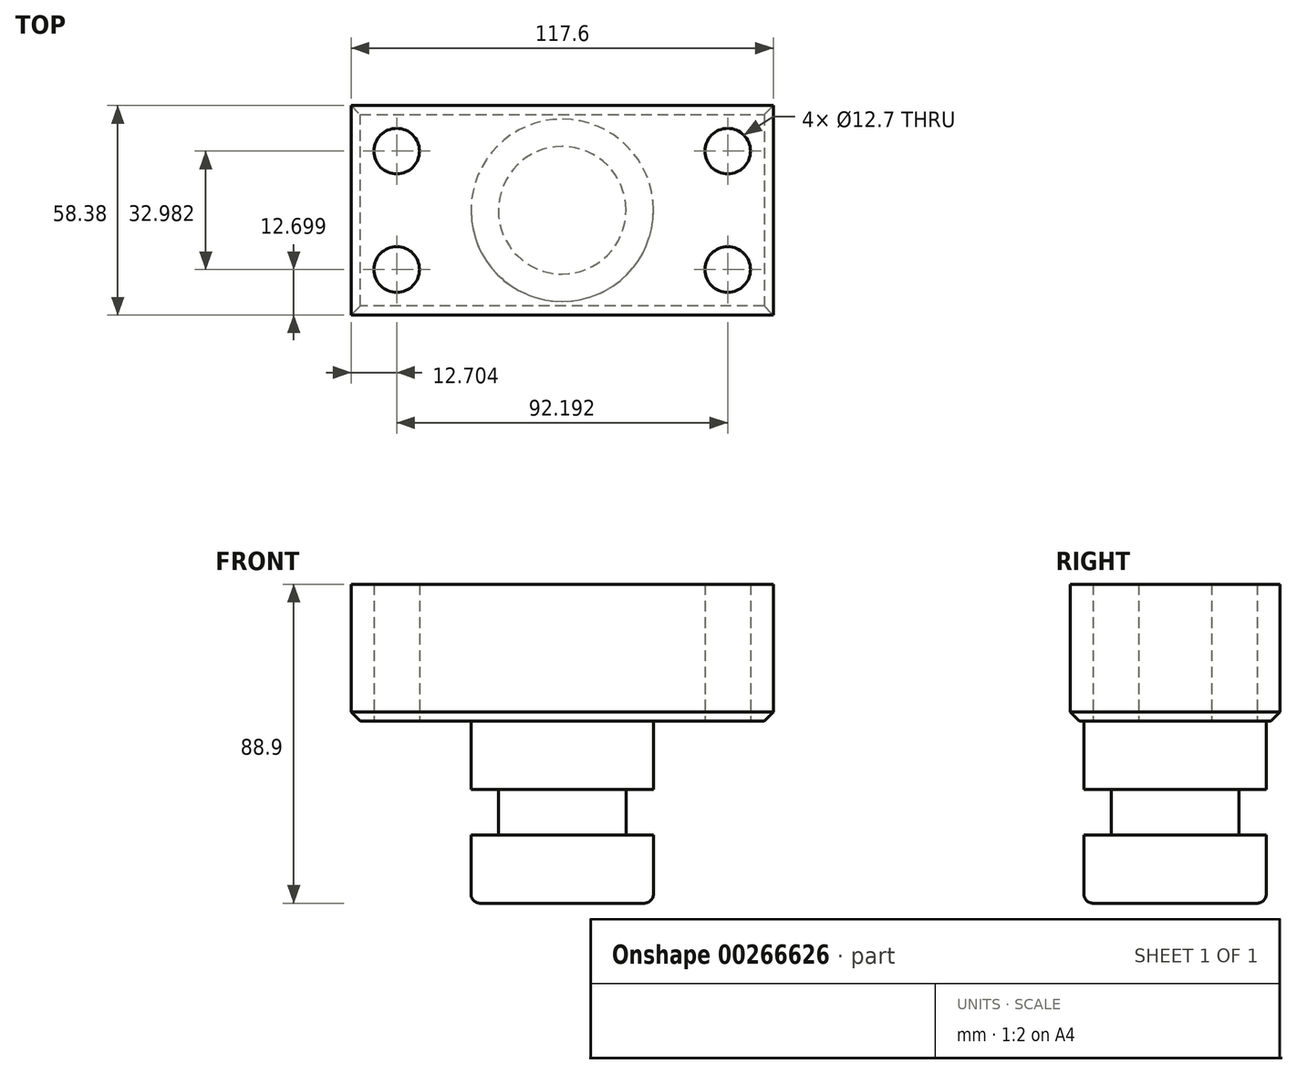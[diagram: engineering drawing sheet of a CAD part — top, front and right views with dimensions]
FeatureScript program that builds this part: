
annotation { "Feature Type Name" : "Feature", "Feature Type Description" : "" }
export const myFeature = defineFeature(function(context is Context, id is Id, definition is map)
    precondition{}
    {
        {
            var Q0;
            Q0=qCreatedBy(makeId("Top.planeOp"),FACE);
            var sketch = newSketch(context, id + "F0", { "sketchPlane" : qUnion([Q0])});
            skLineSegment(sketch, "E0.bottom", {"start": v(-58.8, 29.2) * mm, "end": v(58.8, 29.2) * mm});
            skLineSegment(sketch, "E0.top", {"start": v(-58.8, -29.2) * mm, "end": v(58.8, -29.2) * mm});
            skLineSegment(sketch, "E0.left", {"start": v(-58.8, 29.2) * mm, "end": v(-58.8, -29.2) * mm});
            skLineSegment(sketch, "E0.right", {"start": v(58.8, 29.2) * mm, "end": v(58.8, -29.2) * mm});
            skPoint(sketch, "E0.middle", {"position": v(0, 0) * mm});
            skSolve(sketch);
        }
        {
            var Q0;
            Q0=makeQuery(id+"F0.imprint","IMPRINT",FACE,{"disambiguationData":[TD([[makeQuery(id+"F0.imprint","IMPRINT",EDGE,{"derivedFrom":sQuery(id+"F0.wireOp",EDGE,"E0.bottom")}),-1.0]])]});
            extrude(context, id + "F1", {"entities" : qUnion([Q0]), "oppositeDirection" : true, "depth" : 38.1 * mm});
        }
        {
            var Q0;
            Q0=makeQuery(id+"F1.opExtrude","CAP_FACE",FACE,{"disambiguationData":[OSD([sQuery(id+"F0.wireOp",EDGE,"E0.bottom"),sQuery(id+"F0.wireOp",EDGE,"E0.top"),sQuery(id+"F0.wireOp",EDGE,"E0.left"),sQuery(id+"F0.wireOp",EDGE,"E0.right")])],"isStart":false});
            var sketch = newSketch(context, id + "F2", { "sketchPlane" : qUnion([Q0])});
            skCircle(sketch, "E1", {"center": v(46.1, -16.5) * mm, "radius": 6.35 * mm});
            skCircle(sketch, "E2", {"center": v(-46.1, -16.5) * mm, "radius": 6.35 * mm});
            skCircle(sketch, "E3", {"center": v(-46.1, 16.5) * mm, "radius": 6.35 * mm});
            skCircle(sketch, "E4", {"center": v(46.1, 16.5) * mm, "radius": 6.35 * mm});
            skSolve(sketch);
        }
        {
            var Q0;
            Q0=makeQuery(id+"F2.imprint","IMPRINT",FACE,{"disambiguationData":[TD([[makeQuery(id+"F2.imprint","IMPRINT",EDGE,{"derivedFrom":sQuery(id+"F2.wireOp",EDGE,"E1")}),1.0]])]});
            var Q1;
            Q1=makeQuery(id+"F2.imprint","IMPRINT",FACE,{"disambiguationData":[TD([[makeQuery(id+"F2.imprint","IMPRINT",EDGE,{"derivedFrom":sQuery(id+"F2.wireOp",EDGE,"E2")}),1.0]])]});
            var Q2;
            Q2=makeQuery(id+"F2.imprint","IMPRINT",FACE,{"disambiguationData":[TD([[makeQuery(id+"F2.imprint","IMPRINT",EDGE,{"derivedFrom":sQuery(id+"F2.wireOp",EDGE,"E3")}),1.0]])]});
            var Q3;
            Q3=makeQuery(id+"F2.imprint","IMPRINT",FACE,{"disambiguationData":[TD([[makeQuery(id+"F2.imprint","IMPRINT",EDGE,{"derivedFrom":sQuery(id+"F2.wireOp",EDGE,"E4")}),1.0]])]});
            extrude(context, id + "F3", {"entities" : qUnion([Q0, Q1, Q2, Q3]), "operationType" : NewBodyOperationType.REMOVE, "oppositeDirection" : true, "depth" : 38.1 * mm});
        }
        {
            var Q0;
            Q0=qCreatedBy(makeId("Front.planeOp"),FACE);
            var sketch = newSketch(context, id + "F4", { "sketchPlane" : qUnion([Q0])});
            skLineSegment(sketch, "E5.bottom", {"start": v(0, -88.9) * mm, "end": v(25.4, -88.9) * mm});
            skLineSegment(sketch, "E5.top", {"start": v(0, -38.1) * mm, "end": v(25.4, -38.1) * mm});
            skLineSegment(sketch, "E5.left", {"start": v(0, -88.9) * mm, "end": v(0, -38.1) * mm});
            skLineSegment(sketch, "E5.right", {"start": v(25.4, -88.9) * mm, "end": v(25.4, -38.1) * mm});
            skSolve(sketch);
        }
        {
            var Q0;
            Q0=makeQuery(id+"F4.imprint","IMPRINT",FACE,{"disambiguationData":[TD([[makeQuery(id+"F4.imprint","IMPRINT",EDGE,{"derivedFrom":sQuery(id+"F4.wireOp",EDGE,"E5.bottom")}),1.0]])]});
            var Q1;
            Q1=sQuery(id+"F4.wireOp",EDGE,"E5.left");
            revolve(context, id + "F5", {"operationType" : NewBodyOperationType.ADD, "entities" : qUnion([Q0]), "axis" : qUnion([Q1]), "revolveType" : RevolveType.FULL});
        }
        {
            var Q0;
            Q0=qCreatedBy(makeId("Front.planeOp"),FACE);
            var sketch = newSketch(context, id + "F6", { "sketchPlane" : qUnion([Q0])});
            skLineSegment(sketch, "E6.bottom", {"start": v(-40.4, -69.85) * mm, "end": v(-17.78, -69.85) * mm});
            skLineSegment(sketch, "E6.top", {"start": v(-40.4, -57.15) * mm, "end": v(-17.78, -57.15) * mm});
            skLineSegment(sketch, "E6.left", {"start": v(-40.4, -69.85) * mm, "end": v(-40.4, -57.15) * mm});
            skLineSegment(sketch, "E6.right", {"start": v(-17.78, -69.85) * mm, "end": v(-17.78, -57.15) * mm});
            skSolve(sketch);
        }
        {
            var Q0;
            Q0=makeQuery(id+"F6.imprint","IMPRINT",FACE,{"disambiguationData":[TD([[makeQuery(id+"F6.imprint","IMPRINT",EDGE,{"derivedFrom":sQuery(id+"F6.wireOp",EDGE,"E6.bottom")}),1.0]])]});
            var Q1;
            Q1=makeQuery(id+"F5.opRevolve","SWEPT_EDGE",EDGE,{"disambiguationData":[OSD([sQuery(id+"F4.wireOp",EDGE,"E5.bottom"),sQuery(id+"F4.wireOp",EDGE,"E5.right")])]});
            revolve(context, id + "F7", {"operationType" : NewBodyOperationType.REMOVE, "entities" : qUnion([Q0]), "axis" : qUnion([Q1]), "revolveType" : RevolveType.FULL, "oppositeDirection" : true});
        }
        {
            var Q0;
            Q0=makeQuery(id+"F5.opRevolve","SWEPT_EDGE",EDGE,{"disambiguationData":[OSD([sQuery(id+"F4.wireOp",EDGE,"E5.top"),sQuery(id+"F4.wireOp",EDGE,"E5.right")])]});
            var Q1;
            Q1=makeQuery(id+"F5.opRevolve","SWEPT_EDGE",EDGE,{"disambiguationData":[OSD([sQuery(id+"F4.wireOp",EDGE,"E5.bottom"),sQuery(id+"F4.wireOp",EDGE,"E5.right")])]});
            fillet(context, id + "F8", {"entities" : qUnion([Q0, Q1]), "radius" : 2.54 * mm, "tangentPropagation" : true, "allowEdgeOverflow" : false});
        }
        {
            var Q0;
            Q0=makeQuery(id+"F1.opExtrude","CAP_EDGE",EDGE,{"disambiguationData":[OSD([sQuery(id+"F0.wireOp",EDGE,"E0.top")])],"isStart":false});
            var Q1;
            Q1=makeQuery(id+"F1.opExtrude","CAP_EDGE",EDGE,{"disambiguationData":[OSD([sQuery(id+"F0.wireOp",EDGE,"E0.bottom")])],"isStart":false});
            var Q2;
            Q2=makeQuery(id+"F1.opExtrude","CAP_EDGE",EDGE,{"disambiguationData":[OSD([sQuery(id+"F0.wireOp",EDGE,"E0.bottom")])],"isStart":false});
            var Q3;
            Q3=makeQuery(id+"F1.opExtrude","CAP_EDGE",EDGE,{"disambiguationData":[OSD([sQuery(id+"F0.wireOp",EDGE,"E0.left")])],"isStart":false});
            var Q4;
            Q4=makeQuery(id+"F1.opExtrude","CAP_EDGE",EDGE,{"disambiguationData":[OSD([sQuery(id+"F0.wireOp",EDGE,"E0.right")])],"isStart":false});
            chamfer(context, id + "F9", {"entities" : qUnion([Q0, Q1, Q2, Q3, Q4]), "width" : 2.54 * mm, "tangentPropagation" : true});
        }
    });
